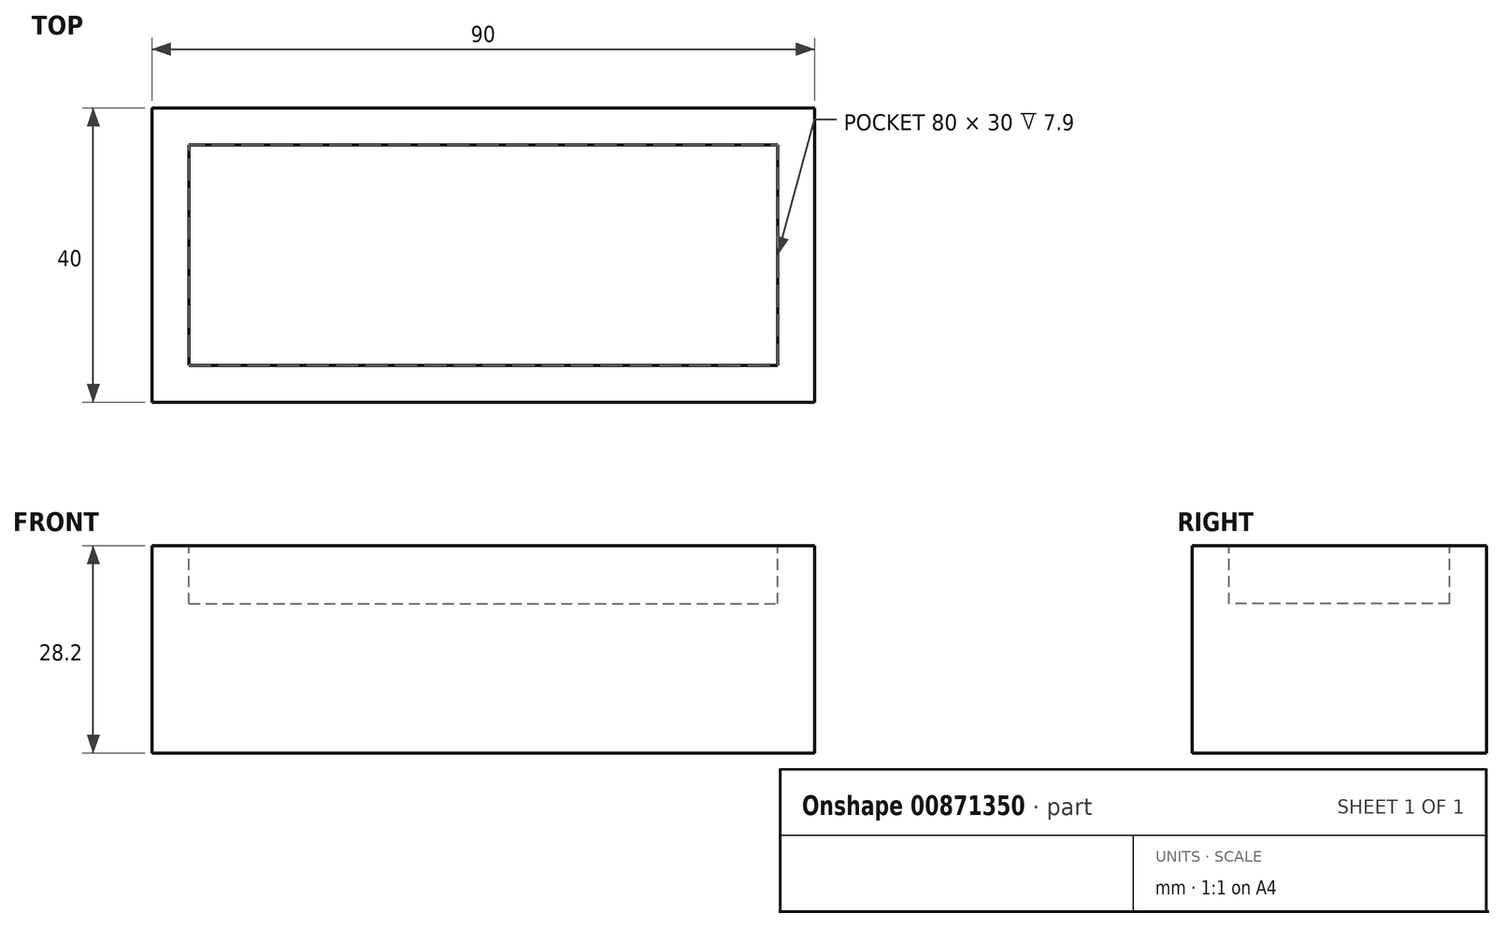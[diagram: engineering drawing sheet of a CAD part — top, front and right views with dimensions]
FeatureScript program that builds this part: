
annotation { "Feature Type Name" : "Feature", "Feature Type Description" : "" }
export const myFeature = defineFeature(function(context is Context, id is Id, definition is map)
    precondition{}
    {
        {
            var Q0;
            Q0=qCreatedBy(makeId("Top.planeOp"),FACE);
            var sketch = newSketch(context, id + "F0", { "sketchPlane" : qUnion([Q0])});
            skLineSegment(sketch, "E0.bottom", {"start": v(-45, 20) * mm, "end": v(45, 20) * mm});
            skLineSegment(sketch, "E0.top", {"start": v(-45, -20) * mm, "end": v(45, -20) * mm});
            skLineSegment(sketch, "E0.left", {"start": v(-45, 20) * mm, "end": v(-45, -20) * mm});
            skLineSegment(sketch, "E0.right", {"start": v(45, 20) * mm, "end": v(45, -20) * mm});
            skPoint(sketch, "E1", {"position": v(0, 20) * mm});
            skPoint(sketch, "E2", {"position": v(0, -20) * mm});
            skPoint(sketch, "E3", {"position": v(-45, 0) * mm});
            skPoint(sketch, "E4", {"position": v(45, 0) * mm});
            skSolve(sketch);
        }
        {
            var Q0;
            Q0=makeQuery(id+"F0.imprint","IMPRINT",FACE,{"disambiguationData":[TD([[makeQuery(id+"F0.imprint","IMPRINT",EDGE,{"derivedFrom":sQuery(id+"F0.wireOp",EDGE,"E0.bottom")}),-1.0]])]});
            extrude(context, id + "F1", {"entities" : qUnion([Q0]), "depth" : 28.2 * mm, "offsetDistance" : 25 * mm});
        }
        {
            var Q0;
            Q0=makeQuery(id+"F1.opExtrude","CAP_FACE",FACE,{"disambiguationData":[OSD([sQuery(id+"F0.wireOp",EDGE,"E0.bottom"),sQuery(id+"F0.wireOp",EDGE,"E0.top"),sQuery(id+"F0.wireOp",EDGE,"E0.left"),sQuery(id+"F0.wireOp",EDGE,"E0.right")])],"isStart":false});
            var sketch = newSketch(context, id + "F2", { "sketchPlane" : qUnion([Q0])});
            skLineSegment(sketch, "E5.bottom", {"start": v(-40, 15) * mm, "end": v(40, 15) * mm});
            skLineSegment(sketch, "E5.top", {"start": v(-40, -15) * mm, "end": v(40, -15) * mm});
            skLineSegment(sketch, "E5.left", {"start": v(-40, 15) * mm, "end": v(-40, -15) * mm});
            skLineSegment(sketch, "E5.right", {"start": v(40, 15) * mm, "end": v(40, -15) * mm});
            skPoint(sketch, "E6", {"position": v(0, 15) * mm});
            skPoint(sketch, "E7", {"position": v(40, 0) * mm});
            skSolve(sketch);
        }
        {
            var Q0;
            Q0=makeQuery(id+"F2.imprint","IMPRINT",FACE,{"disambiguationData":[TD([[makeQuery(id+"F2.imprint","IMPRINT",EDGE,{"derivedFrom":sQuery(id+"F2.wireOp",EDGE,"E5.bottom")}),-1.0]])]});
            extrude(context, id + "F3", {"entities" : qUnion([Q0]), "operationType" : NewBodyOperationType.REMOVE, "oppositeDirection" : true, "depth" : 7.9 * mm, "offsetDistance" : 25 * mm});
        }
    });
